# Revit family: oventrop_hycocon-htz_1068564-72rfa
name_source: partatom
category: Арматура трубопроводов
revit_build: Autodesk Revit 2017 (Build: 20160225_1515(x64)
units: mm (PartAtom-declared; Revit-internal decimal feet)

## family parameters
Всегда вертикально = Да
Заголовок OmniClass = Adjusting/Controlling Valves for Liquid Services
На основе рабочей плоскости = Нет
Номер OmniClass = 23.65.55.14.17
Общий = Нет
При загрузке вырезать с полостями = Нет
Размер круглого соединителя = Использовать радиус
Тип детали = Клапан - Вставляется

## types (5) — shared parameters
Angle = 55.00°
Article Description = Regulating valve
Article Type = Hycocon HTZ 10685
Black = Color RGB 35-35-35
Brass = Color RGB 168-128-48
Custom = Нет
EMCS Version = 2.0
ETIM Article Class = EC011435
Family Version = 10.14
IFCExportAs = IfcValveType
IFCExportType = REGULATING
MEPcontent Class = VALVE_CONTROL
Manufacturer URL = http://www.oventrop.de
Pressure Drop = 0.0 Па
Product Line = Oventrop
Rad3 = 13 мм
Rad4 = 15 мм
Rad4_a = 12 мм
Rad5 = 10 мм
Revit Version = 2015
d = 38 мм
Группа модели = Hycocon HTZ 10685
Изготовитель = Oventrop
Описание = Regulating valve

## per-type parameters (varying)
| type | D | GTIN | H1 | H2 | H3 | Height | L1 | Length | Manufacturer Art. No. | Nominal Diameter | Nominal Radius | Nominal_Diameter | Outer_Diameter | Rad1 | Rad2 | SW | SW2 | URL | t | t2 |
| DN 15 | 21 мм | 4026755264920 | 19 мм | 27 мм | 77 мм | 33 мм | 30 мм | 80 мм | 1068564 | 15 мм | 8 мм | 13 мм | 21 мм | 11 мм | 14 мм | 27 мм | 31 мм | www.stabiplan.com | 13 мм | 3 мм |
| DN 20 | 26 мм | 4026755264937 | 21 мм | 31 мм | 79 мм | 35 мм | 35 мм | 82 мм | 1068566 | 20 мм | 10 мм | 19 мм | 27 мм | 13 мм | 16 мм | 32 мм | 37 мм | http://file-system.ru | 15 мм | 3 мм |
| DN 25 | 33 мм | 4026755264944 | 23 мм | 37 мм | 81 мм | 37 мм | 39 мм | 92 мм | 1068568 | 25 мм | 13 мм | 25 мм | 34 мм | 17 мм | 21 мм | 41 мм | 47 мм | www.stabiplan.com | 17 мм | 3 мм |
| DN 32 | 33 мм | 4026755264951 | 28 мм | 43 мм | 86 мм | 48 мм | 39 мм | 115 мм | 1068570 | 25 мм | 13 мм | 32 мм | 42 мм | 17 мм | 25 мм | 50 мм | 58 мм | www.stabiplan.com | 19 мм | 4 мм |
| DN 40 | 33 мм | 4026755264968 | 30 мм | 47 мм | 88 мм | 55 мм | 39 мм | 130 мм | 1068572 | 25 мм | 13 мм | 38 мм | 48 мм | 17 мм | 28 мм | 55 мм | 64 мм | www.stabiplan.com | 19 мм | 4 мм |

## geometry (parser evidence)
native form markers: Sweep x5
no freeform markers — native parametric forms only
